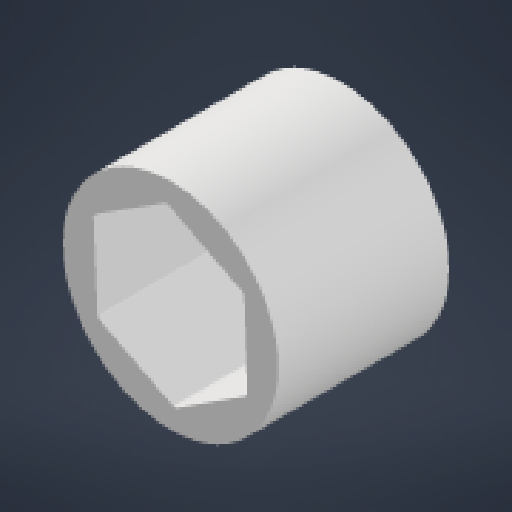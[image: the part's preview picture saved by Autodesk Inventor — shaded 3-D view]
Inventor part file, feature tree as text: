
AUTODESK INVENTOR PART (.ipt)
format: ipt  version: 2024.2 (Build 282272000, 272)  size: 137,728 bytes
history: native  units: in
note: dims shown in document units (in); Inventor stores cm internally (conversion verified against a paired STEP export)
features: sketch x1, plane x1, extrude x1
ambient origin geometry x8: Origin, YZ Plane, XZ Plane, XY Plane, X Axis, Y Axis, Z Axis, Center Point
bodies: Solid1 (feature_tree)
feature tree (3):
  sketch  "Sketch1"  dims[d0=0.3937in d1=1.0in d2=0.0in]
  plane  "Work Plane1"
  extrude  "Extrusion1"  Depth=0.3937in TaperAngle=0.0deg
